# Revit family: CFSCB813EB
name_source: partatom
category: Lighting Fixtures
revit_build: Autodesk Revit Architecture 2012 (Build: 20110309_2315(x64)
units: mm (PartAtom-declared; Revit-internal decimal feet)

## types (1)
- CFSCB813EB
    Bracket = White
    Color Filter = 16777215
    Default Elevation = 48"
    Description = SURFACE CROSS BAFFLE DOWNLIGHT.
    Dimming Lamp Color Temperature Shift = <None>
    Emit from Line Length = 24"
    Flange = Aluminum
    Lamp = TWO
    Length = 48"
    Manufacturer = Prescolite
    Manufacturer Fax = (866)-898-1065
    Model = CFSCB813EB
    Opal lens = Etched Glass
    Photometric Web File = a1551bx.ies
    Product Documentation Link = http://www.prescolite.com
    Product Page URL = http://www.prescolite.com
    Tilt Angle = -90.00°
    URL = www.prescolite.com
    Voltage = 120 V
    Wattage Comments = 13W
    Width = 12"

## geometry (parser evidence)
native form markers: Blend x2, Sweep x3
no freeform markers — native parametric forms only
